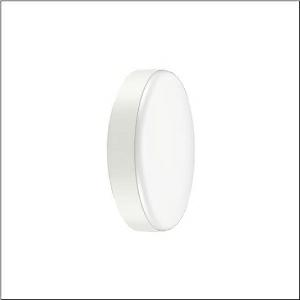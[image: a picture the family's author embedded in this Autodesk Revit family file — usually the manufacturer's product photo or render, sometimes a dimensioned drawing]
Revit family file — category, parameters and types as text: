
# Revit family: rondel_31_51wc10db44as
name_source: partatom
category: Lighting Fixtures
units: mm (PartAtom-declared; Revit-internal decimal feet)

## family parameters
Cut with Voids When Loaded = No
Host = Face
Light Source = No
Part Type = Normal
Room Calculation Point = No
Round Connector Dimension = Use Diameter
Shared = No

## types (1)
- Rondel 31 (1 x LED, 4400 lm, 35.5 W, 4000K)
    Apparent Load = 36 VA
    CIE Flux Codes = 44 75 94 94 100
    Color Rendering = 80
    Color Temperature = 4000K
    Default Elevation = 1800 mm
    Description = Rondel 31, wall and ceiling luminaire, primary optical cover: cover, of PC, opal, light emission: direct distribution, primary light characteristic: symmetric, installation type: surface-mounted, LED, rated luminous flux: 4.250lm, luminous efficacy: 117lm/W, light colour: 840, colour temperature: 4000K, with terminal, 3-pole, max. 2.5mm², mains connection: 220..240V, AC, 50/60Hz, rated input power: 35.5W, luminaire housing, of PC, traffic white (RAL 9016), diameter: 480mm, brightness and presence sensor, HF sensor, protection rating (complete): IP65, insulation class (complete): insulation class II (safety insulation), certification: CE, impact resistance: IK10, permissible storage temperature: -20..+60°C, packaging unit: 1 piece
    Height = 97 mm
    Lamp = 1 x LED
    Lamp Light Flux = 4400 lm
    Lamp Power = 35.5 W
    Lamp count = 1
    Length = 480 mm
    Luminous efficacy = 124 lm/W
    Manufacturer = Siteco
    ModVariant = No
    Model = 51WC10DB44AS
    Mounting Place = Ceiling
    Mounting Type = Surface mounted
    Number of Poles = 1
    OnlyDefault = Yes
    Power Factor = 1
    Product Name = Rondel 31
    Product group = wall and ceiling luminaire
    ProductGroupID = 301
    Protection Class = Protection class II
    Protection Degree = IP 65
    RLX_Detail_Level = 1
    RlxData = <blob elided: 40773 chars, md5=5dd655c1>
    Socket = socket
    Standby Power = 0 W
    System Light Flux = 4400 lm
    System Power = 36 W
    Type Comments = Product without accessories
    Type Image = l_1007188.jpg
    URL = http://relux.com
    VarID = ---
    Voltage = 0 V
    Weight = 0.00 kg
    Width = 0 mm  [stored 0 ft]

note: [stored X ft] marks values corroborated as IEEE doubles in the binary element streams (Revit-internal decimal feet)

## geometry (parser evidence)
native form markers: Blend x4, Sweep x11
no freeform markers — native parametric forms only
